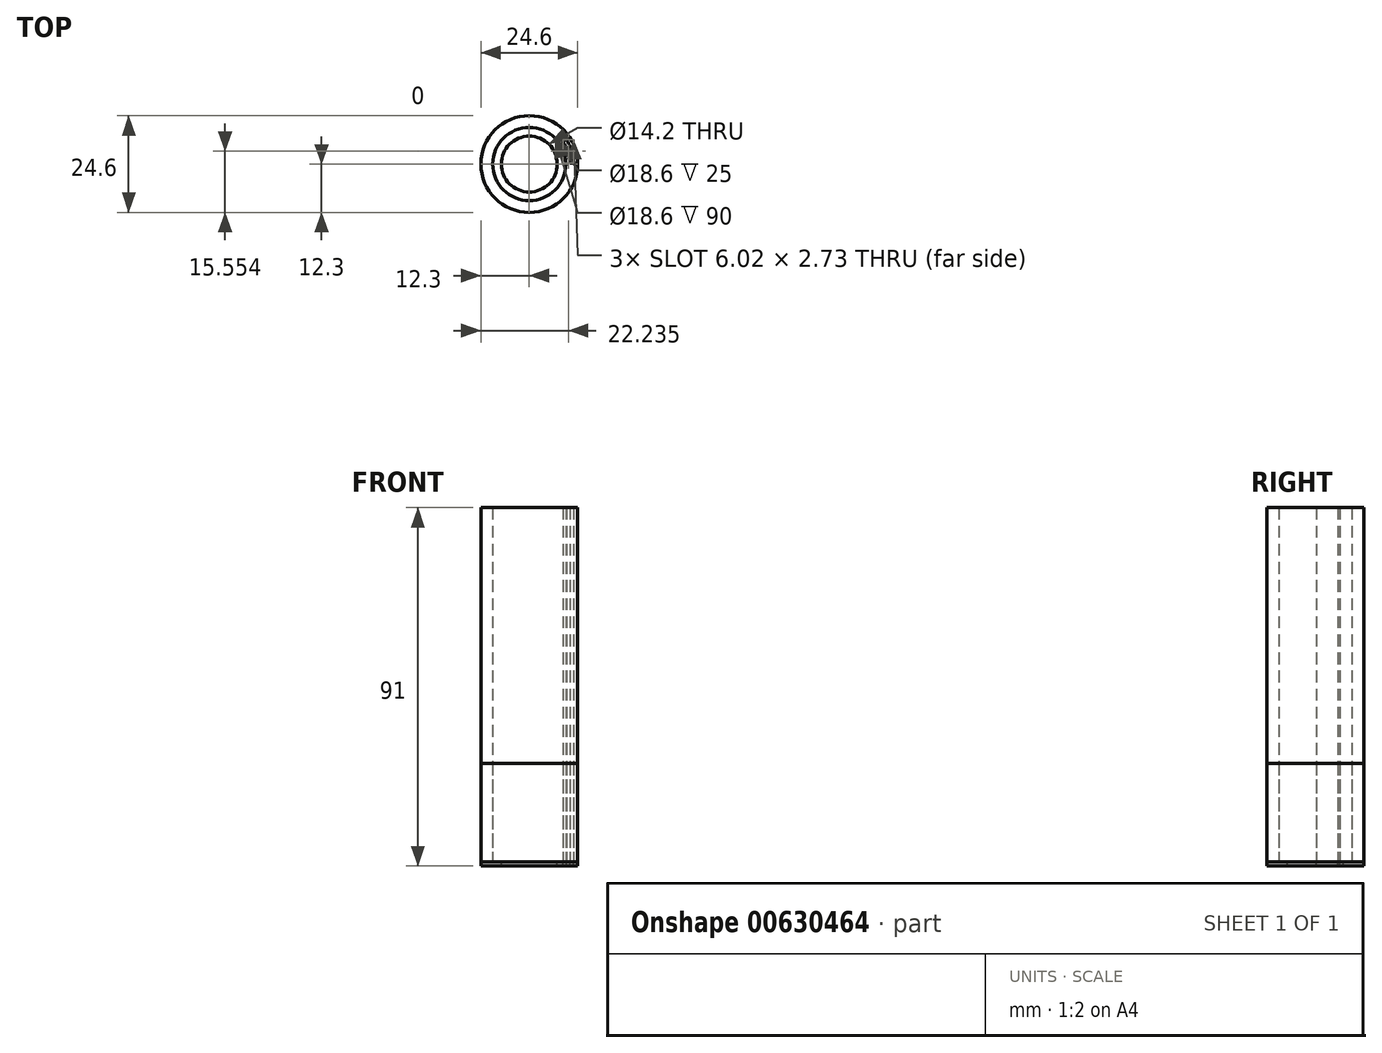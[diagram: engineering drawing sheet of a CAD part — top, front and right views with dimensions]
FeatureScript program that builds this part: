
annotation { "Feature Type Name" : "Feature", "Feature Type Description" : "" }
export const myFeature = defineFeature(function(context is Context, id is Id, definition is map)
    precondition{}
    {
        {
            var Q0;
            Q0=qCreatedBy(makeId("Top.planeOp"),FACE);
            var sketch = newSketch(context, id + "F0", { "sketchPlane" : qUnion([Q0])});
            skCircle(sketch, "E0", {"center": v(0, 0) * mm, "radius": 9.3 * mm});
            skCircle(sketch, "E1", {"center": v(0, 0) * mm, "radius": 12.3 * mm});
            skCircle(sketch, "E2", {"center": v(0, 0) * mm, "radius": 7.1 * mm});
            skLineSegment(sketch, "E3", {"start": v(10.3, 0.24) * mm, "end": v(11.3, 0.24) * mm});
            skArc(sketch, "E4", {"start": v(11.3, 0.24) * mm, "mid": v(10.78, 3.39) * mm, "end": v(9.4, 6.27) * mm});
            skLineSegment(sketch, "E5", {"start": v(8.57, 5.71) * mm, "end": v(9.4, 6.27) * mm});
            skArc(sketch, "E6", {"start": v(10.3, 0.24) * mm, "mid": v(9.82, 3.1) * mm, "end": v(8.57, 5.71) * mm});
            skSolve(sketch);
        }
        {
            var Q0;
            Q0=makeQuery(id+"F0.imprint","IMPRINT",FACE,{"disambiguationData":[TD([[makeQuery(id+"F0.imprint","IMPRINT",EDGE,{"derivedFrom":sQuery(id+"F0.wireOp",EDGE,"E0")}),-1.0]])]});
            extrude(context, id + "F1", {"entities" : qUnion([Q0]), "depth" : 90 * mm, "offsetDistance" : 25 * mm});
        }
        {
            var Q0;
            Q0 = qSketchRegion(id + "F0", true);
            var Q1;
            Q1=makeQuery(id+"F0.imprint","IMPRINT",FACE,{"disambiguationData":[TD([[makeQuery(id+"F0.imprint","IMPRINT",EDGE,{"derivedFrom":sQuery(id+"F0.wireOp",EDGE,"E0")}),1.0]])]});
            extrude(context, id + "F2", {"entities" : qUnion([Q0, Q1]), "oppositeDirection" : true, "depth" : 1 * mm, "offsetDistance" : 25 * mm});
        }
        {
            var Q0;
            Q0 = qSketchRegion(id + "F0", true);
            extrude(context, id + "F3", {"entities" : qUnion([Q0]), "depth" : 25 * mm, "offsetDistance" : 25 * mm});
        }
    });
